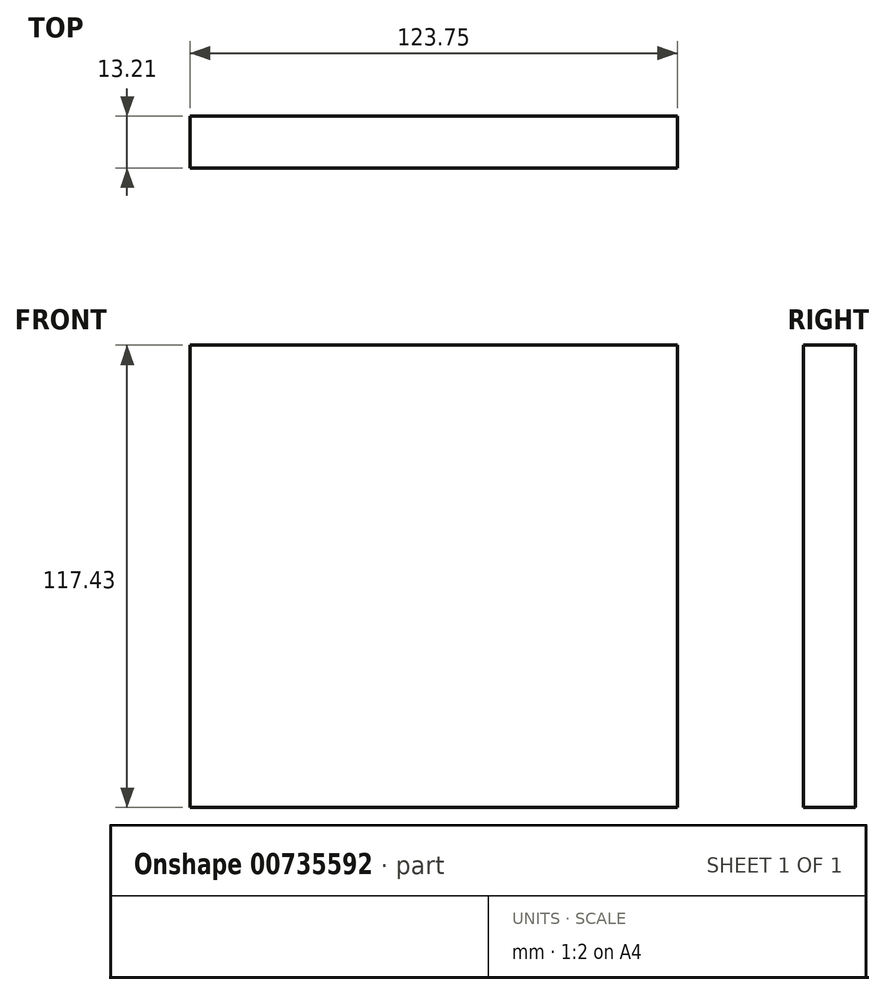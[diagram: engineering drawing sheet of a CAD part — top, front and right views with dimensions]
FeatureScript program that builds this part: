
annotation { "Feature Type Name" : "Feature", "Feature Type Description" : "" }
export const myFeature = defineFeature(function(context is Context, id is Id, definition is map)
    precondition{}
    {
        {
            var Q0;
            Q0=qCreatedBy(makeId("Front.planeOp"),FACE);
            var sketch = newSketch(context, id + "F0", { "sketchPlane" : qUnion([Q0])});
            skLineSegment(sketch, "E0.bottom", {"start": v(-62.02, 58.57) * mm, "end": v(61.73, 58.57) * mm});
            skLineSegment(sketch, "E0.top", {"start": v(-62.02, -58.86) * mm, "end": v(61.73, -58.86) * mm});
            skLineSegment(sketch, "E0.left", {"start": v(-62.02, 58.57) * mm, "end": v(-62.02, -58.86) * mm});
            skLineSegment(sketch, "E0.right", {"start": v(61.73, 58.57) * mm, "end": v(61.73, -58.86) * mm});
            skSolve(sketch);
        }
        {
            var Q0;
            Q0 = qSketchRegion(id + "F0", true);
            extrude(context, id + "F1", {"entities" : qUnion([Q0]), "depth" : 13.2 * mm, "offsetDistance" : 25.4 * mm});
        }
    });
